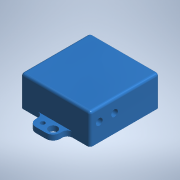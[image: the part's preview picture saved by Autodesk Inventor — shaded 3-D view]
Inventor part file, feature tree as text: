
AUTODESK INVENTOR PART (.ipt)
format: ipt  version: 2022.1 (Build 261234000, 234)  size: 164,352 bytes
history: native  units: mm (DEFAULTED — no unit token found)
features: other x8, extrude x3, sketch x3, fillet x2
bodies: Body1 (feature_tree)
feature tree (16):
  other  "Sólido1"
  other  "Origen"
  extrude  "Extrusión1"  Depth=25.4mm
  extrude  "Extrusión2"  Depth=5.2578mm
  sketch  "Boceto3"  dims[d7=3.175mm d8=1.6002mm d9=1.6002mm d12=30.8356mm d13=1.905mm d14=1.905mm d15=3.81mm d16=3.81mm d17=3.81mm d18=3.81mm d19=1.905mm d20=0.0mm d21=0.9525mm d22=0.9525mm d23=3.7084mm d24=9.2964mm d25=6.477mm d26=6.477mm d27=2.413mm d28=2.6924mm d29=0.0mm]
  fillet  "Empalme1"  Radius=5.2578mm
  fillet  "Empalme2"  Radius=3.175mm
  extrude  "Extrusión3"  Depth=2.6924mm
  other  "Plano YZ"
  other  "Plano XZ"
  other  "Plano XY"
  other  "Eje X"
  other  "Eje Y"
  other  "Eje Z"
  sketch  "Boceto1"  dims[d0=25.4mm d1=25.4mm]
  sketch  "Boceto2"  dims[d2=11.176mm d3=0.0mm d4=5.2578mm d5=5.2578mm d6=3.175mm]
